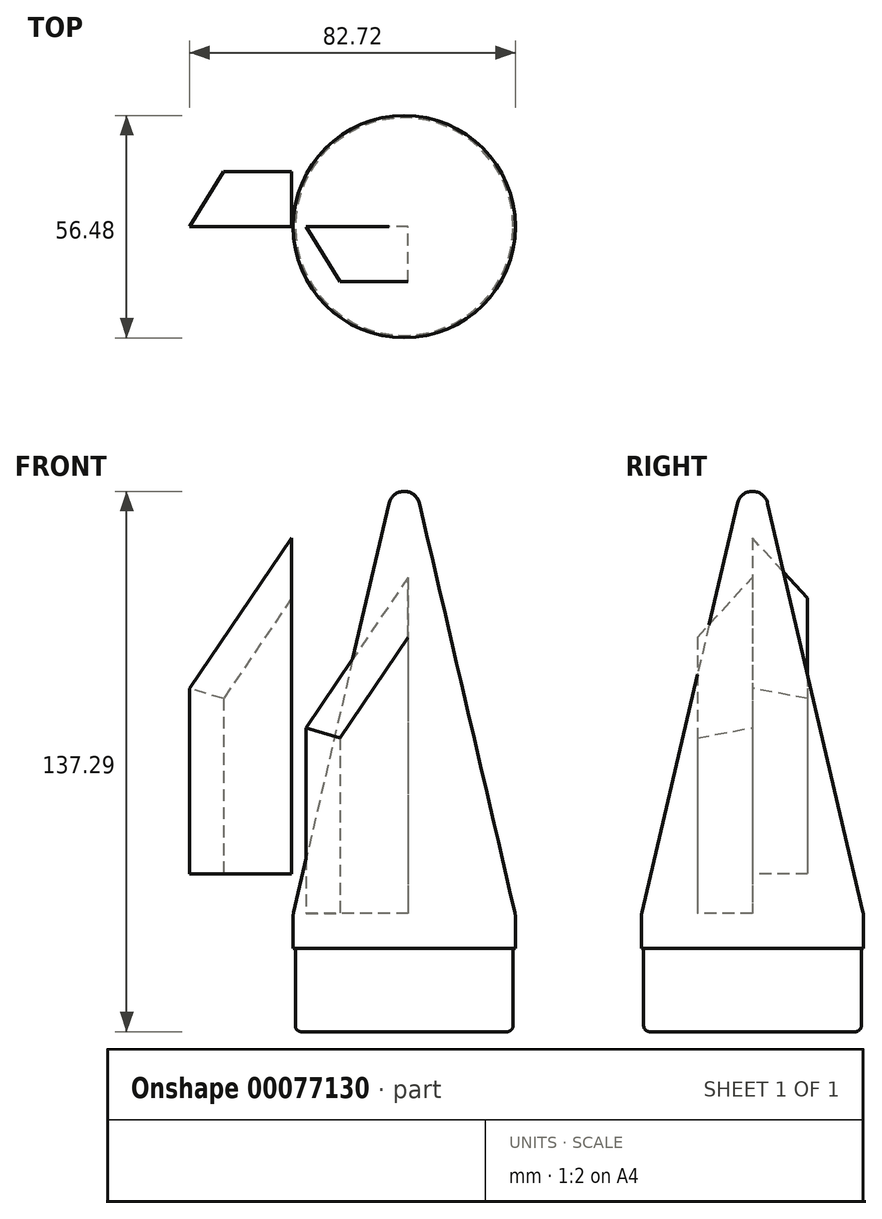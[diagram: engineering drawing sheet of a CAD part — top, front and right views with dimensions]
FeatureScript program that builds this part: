
annotation { "Feature Type Name" : "Feature", "Feature Type Description" : "" }
export const myFeature = defineFeature(function(context is Context, id is Id, definition is map)
    precondition{}
    {
        {
            var Q0;
            Q0=qCreatedBy(makeId("Front.planeOp"),FACE);
            var sketch = newSketch(context, id + "F0", { "sketchPlane" : qUnion([Q0])});
            skLineSegment(sketch, "E0", {"start": v(-33.3, -68.75) * mm, "end": v(-33.3, -68.75) * mm});
            skLineSegment(sketch, "E1", {"start": v(0, -68.75) * mm, "end": v(0, 58.15) * mm});
            skLineSegment(sketch, "E2", {"start": v(0, -68.75) * mm, "end": v(0, -78.75) * mm});
            skLineSegment(sketch, "E3", {"start": v(-32.6, -78.75) * mm, "end": v(-33.3, -78.75) * mm});
            skLineSegment(sketch, "E4", {"start": v(-33.3, -78.75) * mm, "end": v(-33.3, -68.75) * mm});
            skPoint(sketch, "E5.orphan", {"position": v(0, 61.25) * mm});
            skLineSegment(sketch, "E6", {"start": v(-33.3, -68.75) * mm, "end": v(-4.52, 54.56) * mm});
            skLineSegment(sketch, "E7.top", {"start": v(0, -103.75) * mm, "end": v(-32.6, -103.75) * mm});
            skLineSegment(sketch, "E7.left", {"start": v(0, -78.75) * mm, "end": v(0, -103.75) * mm});
            skLineSegment(sketch, "E7.right", {"start": v(-32.6, -78.75) * mm, "end": v(-32.6, -103.75) * mm});
            skArc(sketch, "E8", {"start": v(0, 58.15) * mm, "mid": v(-2.89, 57.15) * mm, "end": v(-4.52, 54.56) * mm});
            skSolve(sketch);
        }
        {
            var Q0;
            {var subQ0=sQuery(id+"F0.wireOp",EDGE,"E2");Q0=makeQuery(id+"F0.imprint","IMPRINT",FACE,{"disambiguationData":[TD([[makeQuery(id+"F0.imprint","IMPRINT",EDGE,{"derivedFrom":subQ0}),-1.0]])]});}
            var Q1;
            Q1=sQuery(id+"F0.wireOp",EDGE,"E1");
            revolve(context, id + "F1", {"entities" : qUnion([Q0]), "axis" : qUnion([Q1]), "revolveType" : RevolveType.FULL});
        }
        {
            var Q0;
            Q0=makeQuery(id+"F1.opRevolve","SWEPT_BODY",BODY,{"disambiguationData":[OSD([sQuery(id+"F0.wireOp",EDGE,"Oh61cgLR-RQo2-T4aV-TcRg-Gp7ijPdUG9jl"),sQuery(id+"F0.wireOp",EDGE,"E1"),sQuery(id+"F0.wireOp",EDGE,"E2"),sQuery(id+"F0.wireOp",EDGE,"E3"),sQuery(id+"F0.wireOp",EDGE,"E4"),sQuery(id+"F0.wireOp",EDGE,"E0"),sQuery(id+"F0.wireOp",EDGE,"dTV1AxgJ-VMAe-DLQO-Zqz3-4UbtDb8FiUJC")])]});
            var Q1;
            Q1=qCreatedBy(makeId("Origin.pointOp"),VERTEX);
            transform(context, id + "F2", {"entities" : qUnion([Q0]), "transformType" : TransformType.SCALE_UNIFORMLY, "scale" : .848, "scalePoint" : qUnion([Q1]), "makeCopy" : false});
        }
        {
            var Q0;
            Q0=qCreatedBy(makeId("Front.planeOp"),FACE);
            var sketch = newSketch(context, id + "F3", { "sketchPlane" : qUnion([Q0])});
            skLineSegment(sketch, "E9", {"start": v(-56.93, -47.9) * mm, "end": v(-56.93, 0) * mm});
            skLineSegment(sketch, "E10", {"start": v(-56.93, 0) * mm, "end": v(-28.6, 41.78) * mm});
            skLineSegment(sketch, "E11", {"start": v(-28.6, 41.78) * mm, "end": v(-28.6, -47.9) * mm});
            skLineSegment(sketch, "E12", {"start": v(-28.6, -47.9) * mm, "end": v(-56.93, -47.9) * mm});
            skSolve(sketch);
        }
        {
            var Q0;
            Q0=makeQuery(id+"F3.imprint","IMPRINT",FACE,{"disambiguationData":[TD([[makeQuery(id+"F3.imprint","IMPRINT",EDGE,{"derivedFrom":sQuery(id+"F3.wireOp",EDGE,"E9")}),-1.0]])]});
            extrude(context, id + "F4", {"entities" : qUnion([Q0]), "depth" : 14 * mm, "offsetDistance" : 25 * mm});
        }
        {
            var Q0;
            Q0=makeQuery(id+"F4.opExtrude","CAP_EDGE",EDGE,{"disambiguationData":[OSD([sQuery(id+"F3.wireOp",EDGE,"E10")])],"isStart":false});
            var Q1;
            Q1=makeQuery(id+"F4.opExtrude","CAP_EDGE",EDGE,{"disambiguationData":[OSD([sQuery(id+"F3.wireOp",EDGE,"E9")])],"isStart":false});
            chamfer(context, id + "F5", {"entities" : qUnion([Q0, Q1]), "chamferType" : ChamferType.TWO_OFFSETS, "width1" : 11 * mm, "oppositeDirection" : false, "width2" : 18 * mm, "tangentPropagation" : true});
        }
        {
            var Q0;
            Q0=makeQuery(id+"F4.opExtrude","SWEPT_BODY",BODY,{"disambiguationData":[OSD([sQuery(id+"F3.wireOp",EDGE,"E9"),sQuery(id+"F3.wireOp",EDGE,"E10"),sQuery(id+"F3.wireOp",EDGE,"E11"),sQuery(id+"F3.wireOp",EDGE,"E12")])]});
            var Q1;
            Q1=qCreatedBy(makeId("Front.planeOp"),FACE);
            mirror(context, id + "F6", {"operationType" : NewBodyOperationType.ADD, "entities" : qUnion([Q0]), "mirrorPlane" : qUnion([Q1])});
        }
        {
            var Q0;
            Q0=makeQuery(id+"F4.opExtrude","SWEPT_BODY",BODY,{"disambiguationData":[OSD([sQuery(id+"F3.wireOp",EDGE,"E9"),sQuery(id+"F3.wireOp",EDGE,"E10"),sQuery(id+"F3.wireOp",EDGE,"E11"),sQuery(id+"F3.wireOp",EDGE,"E12")])]});
            transform(context, id + "F7", {"entities" : qUnion([Q0]), "transformType" : TransformType.TRANSLATION_3D, "dx" : 29.6 * mm, "dy" : 0 * mm, "dz" : -10 * mm, "makeCopy" : false});
        }
        {
            var Q0;
            Q0=makeQuery(id+"F1.opRevolve","SWEPT_EDGE",EDGE,{"disambiguationData":[OSD([sQuery(id+"F0.wireOp",EDGE,"E4"),sQuery(id+"F0.wireOp",EDGE,"E6")])]});
            fillet(context, id + "F8", {"entities" : qUnion([Q0]), "radius" : 5 * mm, "tangentPropagation" : true, "allowEdgeOverflow" : false});
        }
        {
            var Q0;
            Q0=makeQuery(id+"F1.opRevolve","SWEPT_EDGE",EDGE,{"disambiguationData":[OSD([sQuery(id+"F0.wireOp",EDGE,"E7.top"),sQuery(id+"F0.wireOp",EDGE,"E7.right")])]});
            fillet(context, id + "F9", {"entities" : qUnion([Q0]), "radius" : 1.5 * mm, "tangentPropagation" : true, "allowEdgeOverflow" : false});
        }
        {
            var Q0;
            Q0=qCreatedBy(makeId("Top.planeOp"),FACE);
            cPlane(context, id + "F10", {"entities" : qUnion([Q0]), "cplaneType" : CPlaneType.OFFSET, "offset" : 25 * mm, "oppositeDirection" : true, "width" : 150 * mm, "height" : 150 * mm});
        }
        {
            var Q0;
            Q0=qCreatedBy(makeId("Front.planeOp"),FACE);
            cPlane(context, id + "F12", {"entities" : qUnion([Q0]), "cplaneType" : CPlaneType.OFFSET, "offset" : 35 * mm, "width" : 150 * mm, "height" : 150 * mm});
        }
        {
            var Q0;
            Q0=qCreatedBy(id+"F12.planeOp",FACE);
            var sketch = newSketch(context, id + "F13", { "sketchPlane" : qUnion([Q0])});
            skText(sketch, "E13", { "text": "DC3Dparts", "fontName": "OpenSans-Regular.ttf"});
            const initialGuessF13  = {"E13": [-0.024, -0.07859, 1, 0, 0.007]};
            skSetInitialGuess(sketch, initialGuessF13);
            skSolve(sketch);
        }
        {
            var Q0;
            Q0=qSketchRegion(id+"F13",true);
            var Q1;
            Q1=qCreatedBy(makeId("Front.planeOp"),FACE);
            extrude(context, id + "F14", {"entities" : qUnion([Q0]), "endBound" : BoundingType.UP_TO_SURFACE, "oppositeDirection" : true, "depth" : 25 * mm, "endBoundEntityFace" : qUnion([Q1]), "offsetDistance" : 25 * mm});
        }
        {
            var Q0;
            Q0=qCreatedBy(makeId("Front.planeOp"),FACE);
            var sketch = newSketch(context, id + "F15", { "sketchPlane" : qUnion([Q0])});
            skLineSegment(sketch, "E14.bottom", {"start": v(0, -64.71) * mm, "end": v(-27, -64.71) * mm});
            skLineSegment(sketch, "E14.top", {"start": v(0, -103.72) * mm, "end": v(-27, -103.72) * mm});
            skLineSegment(sketch, "E14.left", {"start": v(0, -64.71) * mm, "end": v(0, -103.72) * mm});
            skLineSegment(sketch, "E14.right", {"start": v(-27, -64.71) * mm, "end": v(-27, -103.72) * mm});
            skSolve(sketch);
        }
        {
            var Q0;
            Q0=makeQuery(id+"F15.imprint","IMPRINT",FACE,{"disambiguationData":[TD([[makeQuery(id+"F15.imprint","IMPRINT",EDGE,{"derivedFrom":sQuery(id+"F15.wireOp",EDGE,"E14.bottom")}),1.0]])]});
            var Q1;
            Q1=sQuery(id+"F15.wireOp",EDGE,"E14.left");
            revolve(context, id + "F16", {"entities" : qUnion([Q0]), "axis" : qUnion([Q1]), "revolveType" : RevolveType.FULL});
        }
        {
            var Q0;
            Q0=makeQuery(id+"F16.opRevolve","SWEPT_BODY",BODY,{"disambiguationData":[OSD([sQuery(id+"F15.wireOp",EDGE,"E14.bottom"),sQuery(id+"F15.wireOp",EDGE,"E14.top"),sQuery(id+"F15.wireOp",EDGE,"E14.left"),sQuery(id+"F15.wireOp",EDGE,"E14.right")])]});
            var Q1;
            Q1=makeQuery(id+"F14.opExtrude","SWEPT_BODY",BODY,{"disambiguationData":[OSD([sQuery(id+"F13.wireOp",EDGE,"E13.sketch_text.stroke-0"),sQuery(id+"F13.wireOp",EDGE,"E13.sketch_text.stroke-1"),sQuery(id+"F13.wireOp",EDGE,"E13.sketch_text.stroke-2"),sQuery(id+"F13.wireOp",EDGE,"E13.sketch_text.stroke-3"),sQuery(id+"F13.wireOp",EDGE,"E13.sketch_text.stroke-4"),sQuery(id+"F13.wireOp",EDGE,"E13.sketch_text.stroke-5"),sQuery(id+"F13.wireOp",EDGE,"E13.sketch_text.stroke-6"),sQuery(id+"F13.wireOp",EDGE,"E13.sketch_text.stroke-7"),sQuery(id+"F13.wireOp",EDGE,"E13.sketch_text.stroke-8"),sQuery(id+"F13.wireOp",EDGE,"E13.sketch_text.stroke-9"),sQuery(id+"F13.wireOp",EDGE,"E13.sketch_text.stroke-10"),sQuery(id+"F13.wireOp",EDGE,"E13.sketch_text.stroke-11"),sQuery(id+"F13.wireOp",EDGE,"E13.sketch_text.stroke-12"),sQuery(id+"F13.wireOp",EDGE,"E13.sketch_text.stroke-13")])]});
            var Q2;
            Q2=makeQuery(id+"F14.opExtrude","SWEPT_BODY",BODY,{"disambiguationData":[OSD([sQuery(id+"F13.wireOp",EDGE,"E13.sketch_text.stroke-14"),sQuery(id+"F13.wireOp",EDGE,"E13.sketch_text.stroke-15"),sQuery(id+"F13.wireOp",EDGE,"E13.sketch_text.stroke-16"),sQuery(id+"F13.wireOp",EDGE,"E13.sketch_text.stroke-17"),sQuery(id+"F13.wireOp",EDGE,"E13.sketch_text.stroke-18"),sQuery(id+"F13.wireOp",EDGE,"E13.sketch_text.stroke-19"),sQuery(id+"F13.wireOp",EDGE,"E13.sketch_text.stroke-20"),sQuery(id+"F13.wireOp",EDGE,"E13.sketch_text.stroke-21"),sQuery(id+"F13.wireOp",EDGE,"E13.sketch_text.stroke-22"),sQuery(id+"F13.wireOp",EDGE,"E13.sketch_text.stroke-23"),sQuery(id+"F13.wireOp",EDGE,"E13.sketch_text.stroke-24"),sQuery(id+"F13.wireOp",EDGE,"E13.sketch_text.stroke-25"),sQuery(id+"F13.wireOp",EDGE,"E13.sketch_text.stroke-26"),sQuery(id+"F13.wireOp",EDGE,"E13.sketch_text.stroke-27"),sQuery(id+"F13.wireOp",EDGE,"E13.sketch_text.stroke-28")])]});
            var Q3;
            Q3=makeQuery(id+"F14.opExtrude","SWEPT_BODY",BODY,{"disambiguationData":[OSD([sQuery(id+"F13.wireOp",EDGE,"E13.sketch_text.stroke-29"),sQuery(id+"F13.wireOp",EDGE,"E13.sketch_text.stroke-30"),sQuery(id+"F13.wireOp",EDGE,"E13.sketch_text.stroke-31"),sQuery(id+"F13.wireOp",EDGE,"E13.sketch_text.stroke-32"),sQuery(id+"F13.wireOp",EDGE,"E13.sketch_text.stroke-33"),sQuery(id+"F13.wireOp",EDGE,"E13.sketch_text.stroke-34"),sQuery(id+"F13.wireOp",EDGE,"E13.sketch_text.stroke-35"),sQuery(id+"F13.wireOp",EDGE,"E13.sketch_text.stroke-36"),sQuery(id+"F13.wireOp",EDGE,"E13.sketch_text.stroke-37"),sQuery(id+"F13.wireOp",EDGE,"E13.sketch_text.stroke-38"),sQuery(id+"F13.wireOp",EDGE,"E13.sketch_text.stroke-39"),sQuery(id+"F13.wireOp",EDGE,"E13.sketch_text.stroke-40"),sQuery(id+"F13.wireOp",EDGE,"E13.sketch_text.stroke-41"),sQuery(id+"F13.wireOp",EDGE,"E13.sketch_text.stroke-42"),sQuery(id+"F13.wireOp",EDGE,"E13.sketch_text.stroke-43"),sQuery(id+"F13.wireOp",EDGE,"E13.sketch_text.stroke-44"),sQuery(id+"F13.wireOp",EDGE,"E13.sketch_text.stroke-45"),sQuery(id+"F13.wireOp",EDGE,"E13.sketch_text.stroke-46"),sQuery(id+"F13.wireOp",EDGE,"E13.sketch_text.stroke-47"),sQuery(id+"F13.wireOp",EDGE,"E13.sketch_text.stroke-48"),sQuery(id+"F13.wireOp",EDGE,"E13.sketch_text.stroke-49"),sQuery(id+"F13.wireOp",EDGE,"E13.sketch_text.stroke-50"),sQuery(id+"F13.wireOp",EDGE,"E13.sketch_text.stroke-51"),sQuery(id+"F13.wireOp",EDGE,"E13.sketch_text.stroke-52"),sQuery(id+"F13.wireOp",EDGE,"E13.sketch_text.stroke-53"),sQuery(id+"F13.wireOp",EDGE,"E13.sketch_text.stroke-54"),sQuery(id+"F13.wireOp",EDGE,"E13.sketch_text.stroke-55"),sQuery(id+"F13.wireOp",EDGE,"E13.sketch_text.stroke-56")])]});
            var Q4;
            Q4=makeQuery(id+"F14.opExtrude","SWEPT_BODY",BODY,{"disambiguationData":[OSD([sQuery(id+"F13.wireOp",EDGE,"E13.sketch_text.stroke-57"),sQuery(id+"F13.wireOp",EDGE,"E13.sketch_text.stroke-58"),sQuery(id+"F13.wireOp",EDGE,"E13.sketch_text.stroke-59"),sQuery(id+"F13.wireOp",EDGE,"E13.sketch_text.stroke-60"),sQuery(id+"F13.wireOp",EDGE,"E13.sketch_text.stroke-61"),sQuery(id+"F13.wireOp",EDGE,"E13.sketch_text.stroke-62"),sQuery(id+"F13.wireOp",EDGE,"E13.sketch_text.stroke-63"),sQuery(id+"F13.wireOp",EDGE,"E13.sketch_text.stroke-64"),sQuery(id+"F13.wireOp",EDGE,"E13.sketch_text.stroke-65"),sQuery(id+"F13.wireOp",EDGE,"E13.sketch_text.stroke-66"),sQuery(id+"F13.wireOp",EDGE,"E13.sketch_text.stroke-67"),sQuery(id+"F13.wireOp",EDGE,"E13.sketch_text.stroke-68"),sQuery(id+"F13.wireOp",EDGE,"E13.sketch_text.stroke-69"),sQuery(id+"F13.wireOp",EDGE,"E13.sketch_text.stroke-70")])]});
            var Q5;
            Q5=makeQuery(id+"F14.opExtrude","SWEPT_BODY",BODY,{"disambiguationData":[OSD([sQuery(id+"F13.wireOp",EDGE,"E13.sketch_text.stroke-71"),sQuery(id+"F13.wireOp",EDGE,"E13.sketch_text.stroke-72"),sQuery(id+"F13.wireOp",EDGE,"E13.sketch_text.stroke-73"),sQuery(id+"F13.wireOp",EDGE,"E13.sketch_text.stroke-74"),sQuery(id+"F13.wireOp",EDGE,"E13.sketch_text.stroke-75"),sQuery(id+"F13.wireOp",EDGE,"E13.sketch_text.stroke-76"),sQuery(id+"F13.wireOp",EDGE,"E13.sketch_text.stroke-77"),sQuery(id+"F13.wireOp",EDGE,"E13.sketch_text.stroke-78"),sQuery(id+"F13.wireOp",EDGE,"E13.sketch_text.stroke-79"),sQuery(id+"F13.wireOp",EDGE,"E13.sketch_text.stroke-80"),sQuery(id+"F13.wireOp",EDGE,"E13.sketch_text.stroke-81"),sQuery(id+"F13.wireOp",EDGE,"E13.sketch_text.stroke-82"),sQuery(id+"F13.wireOp",EDGE,"E13.sketch_text.stroke-83"),sQuery(id+"F13.wireOp",EDGE,"E13.sketch_text.stroke-84"),sQuery(id+"F13.wireOp",EDGE,"E13.sketch_text.stroke-85"),sQuery(id+"F13.wireOp",EDGE,"E13.sketch_text.stroke-86"),sQuery(id+"F13.wireOp",EDGE,"E13.sketch_text.stroke-87"),sQuery(id+"F13.wireOp",EDGE,"E13.sketch_text.stroke-88"),sQuery(id+"F13.wireOp",EDGE,"E13.sketch_text.stroke-89"),sQuery(id+"F13.wireOp",EDGE,"E13.sketch_text.stroke-90"),sQuery(id+"F13.wireOp",EDGE,"E13.sketch_text.stroke-91"),sQuery(id+"F13.wireOp",EDGE,"E13.sketch_text.stroke-92"),sQuery(id+"F13.wireOp",EDGE,"E13.sketch_text.stroke-93"),sQuery(id+"F13.wireOp",EDGE,"E13.sketch_text.stroke-94"),sQuery(id+"F13.wireOp",EDGE,"E13.sketch_text.stroke-95")])]});
            var Q6;
            Q6=makeQuery(id+"F14.opExtrude","SWEPT_BODY",BODY,{"disambiguationData":[OSD([sQuery(id+"F13.wireOp",EDGE,"E13.sketch_text.stroke-96"),sQuery(id+"F13.wireOp",EDGE,"E13.sketch_text.stroke-97"),sQuery(id+"F13.wireOp",EDGE,"E13.sketch_text.stroke-98"),sQuery(id+"F13.wireOp",EDGE,"E13.sketch_text.stroke-99"),sQuery(id+"F13.wireOp",EDGE,"E13.sketch_text.stroke-100"),sQuery(id+"F13.wireOp",EDGE,"E13.sketch_text.stroke-101"),sQuery(id+"F13.wireOp",EDGE,"E13.sketch_text.stroke-102"),sQuery(id+"F13.wireOp",EDGE,"E13.sketch_text.stroke-103"),sQuery(id+"F13.wireOp",EDGE,"E13.sketch_text.stroke-104"),sQuery(id+"F13.wireOp",EDGE,"E13.sketch_text.stroke-105"),sQuery(id+"F13.wireOp",EDGE,"E13.sketch_text.stroke-106"),sQuery(id+"F13.wireOp",EDGE,"E13.sketch_text.stroke-107"),sQuery(id+"F13.wireOp",EDGE,"E13.sketch_text.stroke-108"),sQuery(id+"F13.wireOp",EDGE,"E13.sketch_text.stroke-109"),sQuery(id+"F13.wireOp",EDGE,"E13.sketch_text.stroke-110"),sQuery(id+"F13.wireOp",EDGE,"E13.sketch_text.stroke-111"),sQuery(id+"F13.wireOp",EDGE,"E13.sketch_text.stroke-112"),sQuery(id+"F13.wireOp",EDGE,"E13.sketch_text.stroke-113"),sQuery(id+"F13.wireOp",EDGE,"E13.sketch_text.stroke-114"),sQuery(id+"F13.wireOp",EDGE,"E13.sketch_text.stroke-115"),sQuery(id+"F13.wireOp",EDGE,"E13.sketch_text.stroke-116"),sQuery(id+"F13.wireOp",EDGE,"E13.sketch_text.stroke-117"),sQuery(id+"F13.wireOp",EDGE,"E13.sketch_text.stroke-118"),sQuery(id+"F13.wireOp",EDGE,"E13.sketch_text.stroke-119"),sQuery(id+"F13.wireOp",EDGE,"E13.sketch_text.stroke-120"),sQuery(id+"F13.wireOp",EDGE,"E13.sketch_text.stroke-121"),sQuery(id+"F13.wireOp",EDGE,"E13.sketch_text.stroke-122")])]});
            var Q7;
            Q7=makeQuery(id+"F14.opExtrude","SWEPT_BODY",BODY,{"disambiguationData":[OSD([sQuery(id+"F13.wireOp",EDGE,"E13.sketch_text.stroke-123"),sQuery(id+"F13.wireOp",EDGE,"E13.sketch_text.stroke-124"),sQuery(id+"F13.wireOp",EDGE,"E13.sketch_text.stroke-125"),sQuery(id+"F13.wireOp",EDGE,"E13.sketch_text.stroke-126"),sQuery(id+"F13.wireOp",EDGE,"E13.sketch_text.stroke-127"),sQuery(id+"F13.wireOp",EDGE,"E13.sketch_text.stroke-128"),sQuery(id+"F13.wireOp",EDGE,"E13.sketch_text.stroke-129"),sQuery(id+"F13.wireOp",EDGE,"E13.sketch_text.stroke-130"),sQuery(id+"F13.wireOp",EDGE,"E13.sketch_text.stroke-131"),sQuery(id+"F13.wireOp",EDGE,"E13.sketch_text.stroke-132"),sQuery(id+"F13.wireOp",EDGE,"E13.sketch_text.stroke-133"),sQuery(id+"F13.wireOp",EDGE,"E13.sketch_text.stroke-134"),sQuery(id+"F13.wireOp",EDGE,"E13.sketch_text.stroke-135")])]});
            var Q8;
            Q8=makeQuery(id+"F14.opExtrude","SWEPT_BODY",BODY,{"disambiguationData":[OSD([sQuery(id+"F13.wireOp",EDGE,"E13.sketch_text.stroke-136"),sQuery(id+"F13.wireOp",EDGE,"E13.sketch_text.stroke-137"),sQuery(id+"F13.wireOp",EDGE,"E13.sketch_text.stroke-138"),sQuery(id+"F13.wireOp",EDGE,"E13.sketch_text.stroke-139"),sQuery(id+"F13.wireOp",EDGE,"E13.sketch_text.stroke-140"),sQuery(id+"F13.wireOp",EDGE,"E13.sketch_text.stroke-141"),sQuery(id+"F13.wireOp",EDGE,"E13.sketch_text.stroke-142"),sQuery(id+"F13.wireOp",EDGE,"E13.sketch_text.stroke-143"),sQuery(id+"F13.wireOp",EDGE,"E13.sketch_text.stroke-144"),sQuery(id+"F13.wireOp",EDGE,"E13.sketch_text.stroke-145"),sQuery(id+"F13.wireOp",EDGE,"E13.sketch_text.stroke-146"),sQuery(id+"F13.wireOp",EDGE,"E13.sketch_text.stroke-147"),sQuery(id+"F13.wireOp",EDGE,"E13.sketch_text.stroke-148"),sQuery(id+"F13.wireOp",EDGE,"E13.sketch_text.stroke-149"),sQuery(id+"F13.wireOp",EDGE,"E13.sketch_text.stroke-150"),sQuery(id+"F13.wireOp",EDGE,"E13.sketch_text.stroke-151"),sQuery(id+"F13.wireOp",EDGE,"E13.sketch_text.stroke-152"),sQuery(id+"F13.wireOp",EDGE,"E13.sketch_text.stroke-153"),sQuery(id+"F13.wireOp",EDGE,"E13.sketch_text.stroke-154")])]});
            var Q9;
            Q9=makeQuery(id+"F14.opExtrude","SWEPT_BODY",BODY,{"disambiguationData":[OSD([sQuery(id+"F13.wireOp",EDGE,"E13.sketch_text.stroke-155"),sQuery(id+"F13.wireOp",EDGE,"E13.sketch_text.stroke-156"),sQuery(id+"F13.wireOp",EDGE,"E13.sketch_text.stroke-157"),sQuery(id+"F13.wireOp",EDGE,"E13.sketch_text.stroke-158"),sQuery(id+"F13.wireOp",EDGE,"E13.sketch_text.stroke-159"),sQuery(id+"F13.wireOp",EDGE,"E13.sketch_text.stroke-160"),sQuery(id+"F13.wireOp",EDGE,"E13.sketch_text.stroke-161"),sQuery(id+"F13.wireOp",EDGE,"E13.sketch_text.stroke-162"),sQuery(id+"F13.wireOp",EDGE,"E13.sketch_text.stroke-163"),sQuery(id+"F13.wireOp",EDGE,"E13.sketch_text.stroke-164"),sQuery(id+"F13.wireOp",EDGE,"E13.sketch_text.stroke-165"),sQuery(id+"F13.wireOp",EDGE,"E13.sketch_text.stroke-166"),sQuery(id+"F13.wireOp",EDGE,"E13.sketch_text.stroke-167"),sQuery(id+"F13.wireOp",EDGE,"E13.sketch_text.stroke-168"),sQuery(id+"F13.wireOp",EDGE,"E13.sketch_text.stroke-169"),sQuery(id+"F13.wireOp",EDGE,"E13.sketch_text.stroke-170"),sQuery(id+"F13.wireOp",EDGE,"E13.sketch_text.stroke-171"),sQuery(id+"F13.wireOp",EDGE,"E13.sketch_text.stroke-172"),sQuery(id+"F13.wireOp",EDGE,"E13.sketch_text.stroke-173"),sQuery(id+"F13.wireOp",EDGE,"E13.sketch_text.stroke-174"),sQuery(id+"F13.wireOp",EDGE,"E13.sketch_text.stroke-175"),sQuery(id+"F13.wireOp",EDGE,"E13.sketch_text.stroke-176"),sQuery(id+"F13.wireOp",EDGE,"E13.sketch_text.stroke-177"),sQuery(id+"F13.wireOp",EDGE,"E13.sketch_text.stroke-178"),sQuery(id+"F13.wireOp",EDGE,"E13.sketch_text.stroke-179")])]});
            booleanBodies(context, id + "F17", {"operationType" : BooleanOperationType.SUBTRACTION, "tools" : qUnion([Q0]), "targets" : qUnion([Q1, Q2, Q3, Q4, Q5, Q6, Q7, Q8, Q9])});
        }
        {
            var Q0;
            Q0=makeQuery(id+"F14.opExtrude","SWEPT_BODY",BODY,{"disambiguationData":[OSD([sQuery(id+"F13.wireOp",EDGE,"E13.sketch_text.stroke-0"),sQuery(id+"F13.wireOp",EDGE,"E13.sketch_text.stroke-1"),sQuery(id+"F13.wireOp",EDGE,"E13.sketch_text.stroke-2"),sQuery(id+"F13.wireOp",EDGE,"E13.sketch_text.stroke-3"),sQuery(id+"F13.wireOp",EDGE,"E13.sketch_text.stroke-4"),sQuery(id+"F13.wireOp",EDGE,"E13.sketch_text.stroke-5"),sQuery(id+"F13.wireOp",EDGE,"E13.sketch_text.stroke-6"),sQuery(id+"F13.wireOp",EDGE,"E13.sketch_text.stroke-7"),sQuery(id+"F13.wireOp",EDGE,"E13.sketch_text.stroke-8"),sQuery(id+"F13.wireOp",EDGE,"E13.sketch_text.stroke-9"),sQuery(id+"F13.wireOp",EDGE,"E13.sketch_text.stroke-10"),sQuery(id+"F13.wireOp",EDGE,"E13.sketch_text.stroke-11"),sQuery(id+"F13.wireOp",EDGE,"E13.sketch_text.stroke-12"),sQuery(id+"F13.wireOp",EDGE,"E13.sketch_text.stroke-13")])]});
            var Q1;
            Q1=makeQuery(id+"F14.opExtrude","SWEPT_BODY",BODY,{"disambiguationData":[OSD([sQuery(id+"F13.wireOp",EDGE,"E13.sketch_text.stroke-14"),sQuery(id+"F13.wireOp",EDGE,"E13.sketch_text.stroke-15"),sQuery(id+"F13.wireOp",EDGE,"E13.sketch_text.stroke-16"),sQuery(id+"F13.wireOp",EDGE,"E13.sketch_text.stroke-17"),sQuery(id+"F13.wireOp",EDGE,"E13.sketch_text.stroke-18"),sQuery(id+"F13.wireOp",EDGE,"E13.sketch_text.stroke-19"),sQuery(id+"F13.wireOp",EDGE,"E13.sketch_text.stroke-20"),sQuery(id+"F13.wireOp",EDGE,"E13.sketch_text.stroke-21"),sQuery(id+"F13.wireOp",EDGE,"E13.sketch_text.stroke-22"),sQuery(id+"F13.wireOp",EDGE,"E13.sketch_text.stroke-23"),sQuery(id+"F13.wireOp",EDGE,"E13.sketch_text.stroke-24"),sQuery(id+"F13.wireOp",EDGE,"E13.sketch_text.stroke-25"),sQuery(id+"F13.wireOp",EDGE,"E13.sketch_text.stroke-26"),sQuery(id+"F13.wireOp",EDGE,"E13.sketch_text.stroke-27"),sQuery(id+"F13.wireOp",EDGE,"E13.sketch_text.stroke-28")])]});
            var Q2;
            Q2=makeQuery(id+"F14.opExtrude","SWEPT_BODY",BODY,{"disambiguationData":[OSD([sQuery(id+"F13.wireOp",EDGE,"E13.sketch_text.stroke-29"),sQuery(id+"F13.wireOp",EDGE,"E13.sketch_text.stroke-30"),sQuery(id+"F13.wireOp",EDGE,"E13.sketch_text.stroke-31"),sQuery(id+"F13.wireOp",EDGE,"E13.sketch_text.stroke-32"),sQuery(id+"F13.wireOp",EDGE,"E13.sketch_text.stroke-33"),sQuery(id+"F13.wireOp",EDGE,"E13.sketch_text.stroke-34"),sQuery(id+"F13.wireOp",EDGE,"E13.sketch_text.stroke-35"),sQuery(id+"F13.wireOp",EDGE,"E13.sketch_text.stroke-36"),sQuery(id+"F13.wireOp",EDGE,"E13.sketch_text.stroke-37"),sQuery(id+"F13.wireOp",EDGE,"E13.sketch_text.stroke-38"),sQuery(id+"F13.wireOp",EDGE,"E13.sketch_text.stroke-39"),sQuery(id+"F13.wireOp",EDGE,"E13.sketch_text.stroke-40"),sQuery(id+"F13.wireOp",EDGE,"E13.sketch_text.stroke-41"),sQuery(id+"F13.wireOp",EDGE,"E13.sketch_text.stroke-42"),sQuery(id+"F13.wireOp",EDGE,"E13.sketch_text.stroke-43"),sQuery(id+"F13.wireOp",EDGE,"E13.sketch_text.stroke-44"),sQuery(id+"F13.wireOp",EDGE,"E13.sketch_text.stroke-45"),sQuery(id+"F13.wireOp",EDGE,"E13.sketch_text.stroke-46"),sQuery(id+"F13.wireOp",EDGE,"E13.sketch_text.stroke-47"),sQuery(id+"F13.wireOp",EDGE,"E13.sketch_text.stroke-48"),sQuery(id+"F13.wireOp",EDGE,"E13.sketch_text.stroke-49"),sQuery(id+"F13.wireOp",EDGE,"E13.sketch_text.stroke-50"),sQuery(id+"F13.wireOp",EDGE,"E13.sketch_text.stroke-51"),sQuery(id+"F13.wireOp",EDGE,"E13.sketch_text.stroke-52"),sQuery(id+"F13.wireOp",EDGE,"E13.sketch_text.stroke-53"),sQuery(id+"F13.wireOp",EDGE,"E13.sketch_text.stroke-54"),sQuery(id+"F13.wireOp",EDGE,"E13.sketch_text.stroke-55"),sQuery(id+"F13.wireOp",EDGE,"E13.sketch_text.stroke-56")])]});
            var Q3;
            Q3=makeQuery(id+"F14.opExtrude","SWEPT_BODY",BODY,{"disambiguationData":[OSD([sQuery(id+"F13.wireOp",EDGE,"E13.sketch_text.stroke-57"),sQuery(id+"F13.wireOp",EDGE,"E13.sketch_text.stroke-58"),sQuery(id+"F13.wireOp",EDGE,"E13.sketch_text.stroke-59"),sQuery(id+"F13.wireOp",EDGE,"E13.sketch_text.stroke-60"),sQuery(id+"F13.wireOp",EDGE,"E13.sketch_text.stroke-61"),sQuery(id+"F13.wireOp",EDGE,"E13.sketch_text.stroke-62"),sQuery(id+"F13.wireOp",EDGE,"E13.sketch_text.stroke-63"),sQuery(id+"F13.wireOp",EDGE,"E13.sketch_text.stroke-64"),sQuery(id+"F13.wireOp",EDGE,"E13.sketch_text.stroke-65"),sQuery(id+"F13.wireOp",EDGE,"E13.sketch_text.stroke-66"),sQuery(id+"F13.wireOp",EDGE,"E13.sketch_text.stroke-67"),sQuery(id+"F13.wireOp",EDGE,"E13.sketch_text.stroke-68"),sQuery(id+"F13.wireOp",EDGE,"E13.sketch_text.stroke-69"),sQuery(id+"F13.wireOp",EDGE,"E13.sketch_text.stroke-70")])]});
            var Q4;
            Q4=makeQuery(id+"F14.opExtrude","SWEPT_BODY",BODY,{"disambiguationData":[OSD([sQuery(id+"F13.wireOp",EDGE,"E13.sketch_text.stroke-71"),sQuery(id+"F13.wireOp",EDGE,"E13.sketch_text.stroke-72"),sQuery(id+"F13.wireOp",EDGE,"E13.sketch_text.stroke-73"),sQuery(id+"F13.wireOp",EDGE,"E13.sketch_text.stroke-74"),sQuery(id+"F13.wireOp",EDGE,"E13.sketch_text.stroke-75"),sQuery(id+"F13.wireOp",EDGE,"E13.sketch_text.stroke-76"),sQuery(id+"F13.wireOp",EDGE,"E13.sketch_text.stroke-77"),sQuery(id+"F13.wireOp",EDGE,"E13.sketch_text.stroke-78"),sQuery(id+"F13.wireOp",EDGE,"E13.sketch_text.stroke-79"),sQuery(id+"F13.wireOp",EDGE,"E13.sketch_text.stroke-80"),sQuery(id+"F13.wireOp",EDGE,"E13.sketch_text.stroke-81"),sQuery(id+"F13.wireOp",EDGE,"E13.sketch_text.stroke-82"),sQuery(id+"F13.wireOp",EDGE,"E13.sketch_text.stroke-83"),sQuery(id+"F13.wireOp",EDGE,"E13.sketch_text.stroke-84"),sQuery(id+"F13.wireOp",EDGE,"E13.sketch_text.stroke-85"),sQuery(id+"F13.wireOp",EDGE,"E13.sketch_text.stroke-86"),sQuery(id+"F13.wireOp",EDGE,"E13.sketch_text.stroke-87"),sQuery(id+"F13.wireOp",EDGE,"E13.sketch_text.stroke-88"),sQuery(id+"F13.wireOp",EDGE,"E13.sketch_text.stroke-89"),sQuery(id+"F13.wireOp",EDGE,"E13.sketch_text.stroke-90"),sQuery(id+"F13.wireOp",EDGE,"E13.sketch_text.stroke-91"),sQuery(id+"F13.wireOp",EDGE,"E13.sketch_text.stroke-92"),sQuery(id+"F13.wireOp",EDGE,"E13.sketch_text.stroke-93"),sQuery(id+"F13.wireOp",EDGE,"E13.sketch_text.stroke-94"),sQuery(id+"F13.wireOp",EDGE,"E13.sketch_text.stroke-95")])]});
            var Q5;
            Q5=makeQuery(id+"F14.opExtrude","SWEPT_BODY",BODY,{"disambiguationData":[OSD([sQuery(id+"F13.wireOp",EDGE,"E13.sketch_text.stroke-96"),sQuery(id+"F13.wireOp",EDGE,"E13.sketch_text.stroke-97"),sQuery(id+"F13.wireOp",EDGE,"E13.sketch_text.stroke-98"),sQuery(id+"F13.wireOp",EDGE,"E13.sketch_text.stroke-99"),sQuery(id+"F13.wireOp",EDGE,"E13.sketch_text.stroke-100"),sQuery(id+"F13.wireOp",EDGE,"E13.sketch_text.stroke-101"),sQuery(id+"F13.wireOp",EDGE,"E13.sketch_text.stroke-102"),sQuery(id+"F13.wireOp",EDGE,"E13.sketch_text.stroke-103"),sQuery(id+"F13.wireOp",EDGE,"E13.sketch_text.stroke-104"),sQuery(id+"F13.wireOp",EDGE,"E13.sketch_text.stroke-105"),sQuery(id+"F13.wireOp",EDGE,"E13.sketch_text.stroke-106"),sQuery(id+"F13.wireOp",EDGE,"E13.sketch_text.stroke-107"),sQuery(id+"F13.wireOp",EDGE,"E13.sketch_text.stroke-108"),sQuery(id+"F13.wireOp",EDGE,"E13.sketch_text.stroke-109"),sQuery(id+"F13.wireOp",EDGE,"E13.sketch_text.stroke-110"),sQuery(id+"F13.wireOp",EDGE,"E13.sketch_text.stroke-111"),sQuery(id+"F13.wireOp",EDGE,"E13.sketch_text.stroke-112"),sQuery(id+"F13.wireOp",EDGE,"E13.sketch_text.stroke-113"),sQuery(id+"F13.wireOp",EDGE,"E13.sketch_text.stroke-114"),sQuery(id+"F13.wireOp",EDGE,"E13.sketch_text.stroke-115"),sQuery(id+"F13.wireOp",EDGE,"E13.sketch_text.stroke-116"),sQuery(id+"F13.wireOp",EDGE,"E13.sketch_text.stroke-117"),sQuery(id+"F13.wireOp",EDGE,"E13.sketch_text.stroke-118"),sQuery(id+"F13.wireOp",EDGE,"E13.sketch_text.stroke-119"),sQuery(id+"F13.wireOp",EDGE,"E13.sketch_text.stroke-120"),sQuery(id+"F13.wireOp",EDGE,"E13.sketch_text.stroke-121"),sQuery(id+"F13.wireOp",EDGE,"E13.sketch_text.stroke-122")])]});
            var Q6;
            Q6=makeQuery(id+"F14.opExtrude","SWEPT_BODY",BODY,{"disambiguationData":[OSD([sQuery(id+"F13.wireOp",EDGE,"E13.sketch_text.stroke-123"),sQuery(id+"F13.wireOp",EDGE,"E13.sketch_text.stroke-124"),sQuery(id+"F13.wireOp",EDGE,"E13.sketch_text.stroke-125"),sQuery(id+"F13.wireOp",EDGE,"E13.sketch_text.stroke-126"),sQuery(id+"F13.wireOp",EDGE,"E13.sketch_text.stroke-127"),sQuery(id+"F13.wireOp",EDGE,"E13.sketch_text.stroke-128"),sQuery(id+"F13.wireOp",EDGE,"E13.sketch_text.stroke-129"),sQuery(id+"F13.wireOp",EDGE,"E13.sketch_text.stroke-130"),sQuery(id+"F13.wireOp",EDGE,"E13.sketch_text.stroke-131"),sQuery(id+"F13.wireOp",EDGE,"E13.sketch_text.stroke-132"),sQuery(id+"F13.wireOp",EDGE,"E13.sketch_text.stroke-133"),sQuery(id+"F13.wireOp",EDGE,"E13.sketch_text.stroke-134"),sQuery(id+"F13.wireOp",EDGE,"E13.sketch_text.stroke-135")])]});
            var Q7;
            Q7=makeQuery(id+"F14.opExtrude","SWEPT_BODY",BODY,{"disambiguationData":[OSD([sQuery(id+"F13.wireOp",EDGE,"E13.sketch_text.stroke-136"),sQuery(id+"F13.wireOp",EDGE,"E13.sketch_text.stroke-137"),sQuery(id+"F13.wireOp",EDGE,"E13.sketch_text.stroke-138"),sQuery(id+"F13.wireOp",EDGE,"E13.sketch_text.stroke-139"),sQuery(id+"F13.wireOp",EDGE,"E13.sketch_text.stroke-140"),sQuery(id+"F13.wireOp",EDGE,"E13.sketch_text.stroke-141"),sQuery(id+"F13.wireOp",EDGE,"E13.sketch_text.stroke-142"),sQuery(id+"F13.wireOp",EDGE,"E13.sketch_text.stroke-143"),sQuery(id+"F13.wireOp",EDGE,"E13.sketch_text.stroke-144"),sQuery(id+"F13.wireOp",EDGE,"E13.sketch_text.stroke-145"),sQuery(id+"F13.wireOp",EDGE,"E13.sketch_text.stroke-146"),sQuery(id+"F13.wireOp",EDGE,"E13.sketch_text.stroke-147"),sQuery(id+"F13.wireOp",EDGE,"E13.sketch_text.stroke-148"),sQuery(id+"F13.wireOp",EDGE,"E13.sketch_text.stroke-149"),sQuery(id+"F13.wireOp",EDGE,"E13.sketch_text.stroke-150"),sQuery(id+"F13.wireOp",EDGE,"E13.sketch_text.stroke-151"),sQuery(id+"F13.wireOp",EDGE,"E13.sketch_text.stroke-152"),sQuery(id+"F13.wireOp",EDGE,"E13.sketch_text.stroke-153"),sQuery(id+"F13.wireOp",EDGE,"E13.sketch_text.stroke-154")])]});
            var Q8;
            Q8=makeQuery(id+"F14.opExtrude","SWEPT_BODY",BODY,{"disambiguationData":[OSD([sQuery(id+"F13.wireOp",EDGE,"E13.sketch_text.stroke-155"),sQuery(id+"F13.wireOp",EDGE,"E13.sketch_text.stroke-156"),sQuery(id+"F13.wireOp",EDGE,"E13.sketch_text.stroke-157"),sQuery(id+"F13.wireOp",EDGE,"E13.sketch_text.stroke-158"),sQuery(id+"F13.wireOp",EDGE,"E13.sketch_text.stroke-159"),sQuery(id+"F13.wireOp",EDGE,"E13.sketch_text.stroke-160"),sQuery(id+"F13.wireOp",EDGE,"E13.sketch_text.stroke-161"),sQuery(id+"F13.wireOp",EDGE,"E13.sketch_text.stroke-162"),sQuery(id+"F13.wireOp",EDGE,"E13.sketch_text.stroke-163"),sQuery(id+"F13.wireOp",EDGE,"E13.sketch_text.stroke-164"),sQuery(id+"F13.wireOp",EDGE,"E13.sketch_text.stroke-165"),sQuery(id+"F13.wireOp",EDGE,"E13.sketch_text.stroke-166"),sQuery(id+"F13.wireOp",EDGE,"E13.sketch_text.stroke-167"),sQuery(id+"F13.wireOp",EDGE,"E13.sketch_text.stroke-168"),sQuery(id+"F13.wireOp",EDGE,"E13.sketch_text.stroke-169"),sQuery(id+"F13.wireOp",EDGE,"E13.sketch_text.stroke-170"),sQuery(id+"F13.wireOp",EDGE,"E13.sketch_text.stroke-171"),sQuery(id+"F13.wireOp",EDGE,"E13.sketch_text.stroke-172"),sQuery(id+"F13.wireOp",EDGE,"E13.sketch_text.stroke-173"),sQuery(id+"F13.wireOp",EDGE,"E13.sketch_text.stroke-174"),sQuery(id+"F13.wireOp",EDGE,"E13.sketch_text.stroke-175"),sQuery(id+"F13.wireOp",EDGE,"E13.sketch_text.stroke-176"),sQuery(id+"F13.wireOp",EDGE,"E13.sketch_text.stroke-177"),sQuery(id+"F13.wireOp",EDGE,"E13.sketch_text.stroke-178"),sQuery(id+"F13.wireOp",EDGE,"E13.sketch_text.stroke-179")])]});
            var Q9;
            Q9=makeQuery(id+"F4.opExtrude","SWEPT_BODY",BODY,{"disambiguationData":[OSD([sQuery(id+"F3.wireOp",EDGE,"E9"),sQuery(id+"F3.wireOp",EDGE,"E10"),sQuery(id+"F3.wireOp",EDGE,"E11"),sQuery(id+"F3.wireOp",EDGE,"E12")])]});
            booleanBodies(context, id + "F18", {"operationType" : BooleanOperationType.SUBTRACTION, "tools" : qUnion([Q0, Q1, Q2, Q3, Q4, Q5, Q6, Q7, Q8]), "targets" : qUnion([Q9])});
        }
        {
            var Q0;
            Q0=qCreatedBy(id+"F10.planeOp",FACE);
            var sketch = newSketch(context, id + "F19", { "sketchPlane" : qUnion([Q0])});
            skCircle(sketch, "E15", {"center": v(0, 20.23) * mm, "radius": 2 * mm});
            skSolve(sketch);
        }
        {
            var Q0;
            Q0=makeQuery(id+"F19.imprint","IMPRINT",FACE,{"disambiguationData":[TD([[makeQuery(id+"F19.imprint","IMPRINT",EDGE,{"derivedFrom":sQuery(id+"F19.wireOp",EDGE,"E15")}),1.0]])]});
            extrude(context, id + "F20", {"entities" : qUnion([Q0]), "depth" : 25 * mm, "offsetDistance" : 25 * mm});
        }
        {
            var Q0;
            Q0=makeQuery(id+"F20.opExtrude","CAP_EDGE",EDGE,{"disambiguationData":[OSD([sQuery(id+"F19.wireOp",EDGE,"E15")])],"isStart":true});
            fillet(context, id + "F21", {"entities" : qUnion([Q0]), "radius" : 2 * mm, "tangentPropagation" : true, "allowEdgeOverflow" : false});
        }
        {
            var Q0;
            Q0=makeQuery(id+"F20.opExtrude","SWEPT_BODY",BODY,{"disambiguationData":[OSD([sQuery(id+"F19.wireOp",EDGE,"E15")])]});
            transform(context, id + "F22", {"entities" : qUnion([Q0]), "transformType" : TransformType.TRANSLATION_3D, "dx" : 7 * mm, "dy" : 1.4 * mm, "dz" : -10.6 * mm, "makeCopy" : true});
        }
        {
            var Q0;
            Q0=makeQuery(id+"F20.opExtrude","SWEPT_BODY",BODY,{"disambiguationData":[OSD([sQuery(id+"F19.wireOp",EDGE,"E15")])]});
            var Q1;
            Q1=makeQuery(id+"F22.opPattern","COPY",BODY,{"derivedFrom":makeQuery(id+"F20.opExtrude","SWEPT_BODY",BODY,{"disambiguationData":[OSD([sQuery(id+"F19.wireOp",EDGE,"E15")])]}),"instanceName":"1"});
            var Q2;
            Q2=qCreatedBy(makeId("Front.planeOp"),FACE);
            mirror(context, id + "F23", {"entities" : qUnion([Q0, Q1]), "mirrorPlane" : qUnion([Q2])});
        }
        {
            var Q0;
            Q0=makeQuery(id+"F20.opExtrude","SWEPT_BODY",BODY,{"disambiguationData":[OSD([sQuery(id+"F19.wireOp",EDGE,"E15")])]});
            var Q1;
            Q1=makeQuery(id+"F23.opPattern","COPY",BODY,{"derivedFrom":makeQuery(id+"F20.opExtrude","SWEPT_BODY",BODY,{"disambiguationData":[OSD([sQuery(id+"F19.wireOp",EDGE,"E15")])]}),"instanceName":"1"});
            var Q2;
            Q2=makeQuery(id+"F22.opPattern","COPY",BODY,{"derivedFrom":makeQuery(id+"F20.opExtrude","SWEPT_BODY",BODY,{"disambiguationData":[OSD([sQuery(id+"F19.wireOp",EDGE,"E15")])]}),"instanceName":"1"});
            var Q3;
            Q3=makeQuery(id+"F23.opPattern","COPY",BODY,{"derivedFrom":makeQuery(id+"F22.opPattern","COPY",BODY,{"derivedFrom":makeQuery(id+"F20.opExtrude","SWEPT_BODY",BODY,{"disambiguationData":[OSD([sQuery(id+"F19.wireOp",EDGE,"E15")])]}),"instanceName":"1"}),"instanceName":"1"});
            var Q4;
            Q4=makeQuery(id+"F4.opExtrude","SWEPT_BODY",BODY,{"disambiguationData":[OSD([sQuery(id+"F3.wireOp",EDGE,"E9"),sQuery(id+"F3.wireOp",EDGE,"E10"),sQuery(id+"F3.wireOp",EDGE,"E11"),sQuery(id+"F3.wireOp",EDGE,"E12")])]});
            booleanBodies(context, id + "F24", {"operationType" : BooleanOperationType.SUBTRACTION, "tools" : qUnion([Q0, Q1, Q2, Q3]), "targets" : qUnion([Q4])});
        }
    });
